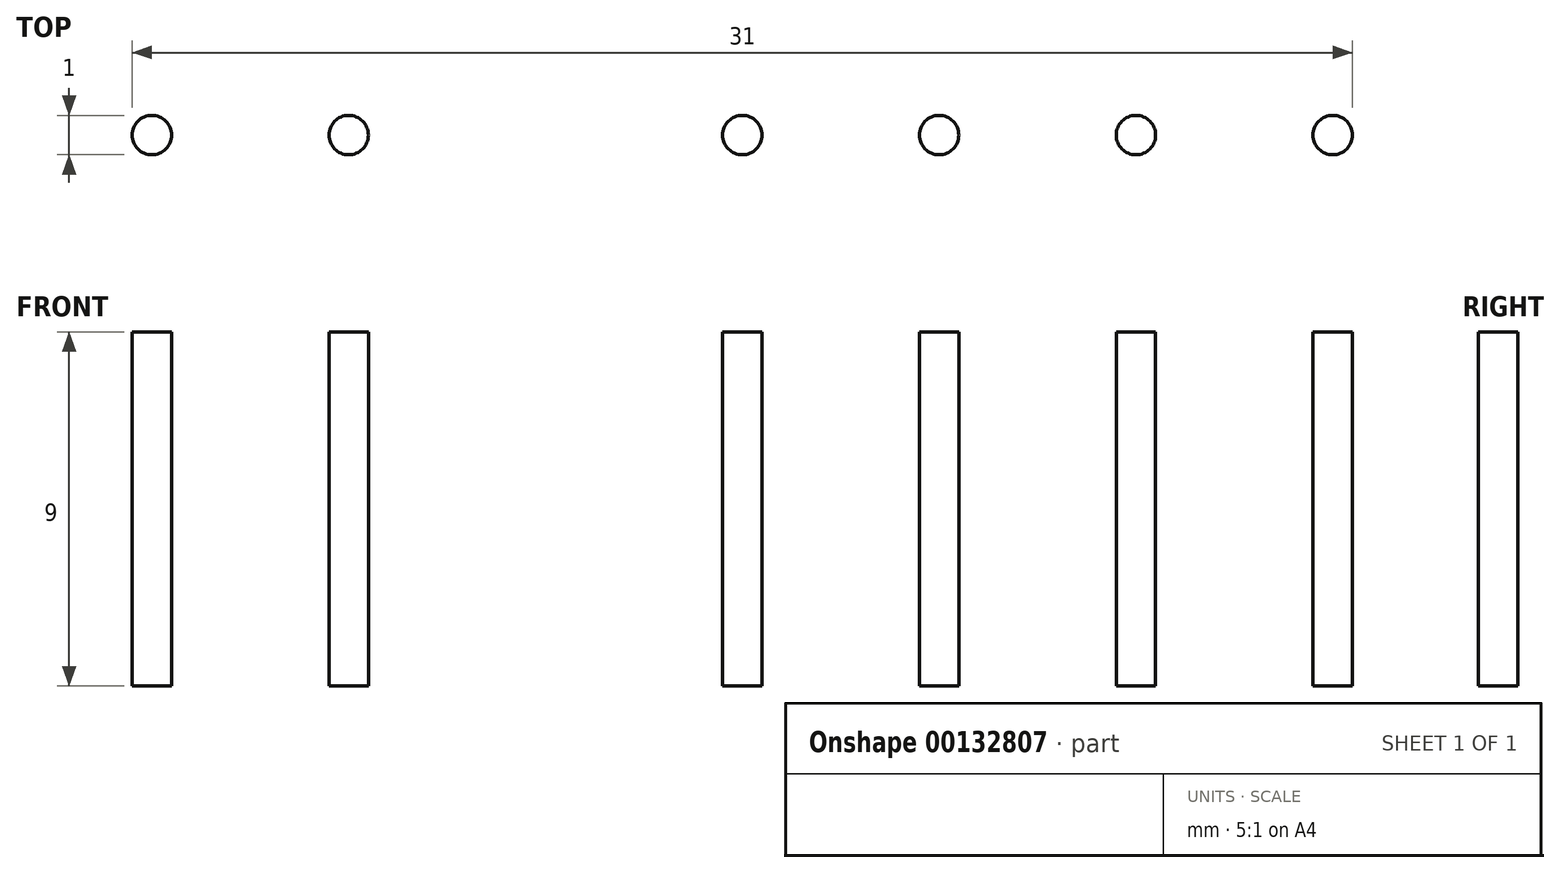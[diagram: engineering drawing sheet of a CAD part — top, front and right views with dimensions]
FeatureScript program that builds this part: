
annotation { "Feature Type Name" : "Feature", "Feature Type Description" : "" }
export const myFeature = defineFeature(function(context is Context, id is Id, definition is map)
    precondition{}
    {
        {
            var Q0;
            Q0=qCreatedBy(makeId("Top.planeOp"),FACE);
            var sketch = newSketch(context, id + "F0", { "sketchPlane" : qUnion([Q0])});
            skCircle(sketch, "E0", {"center": v(0, -20) * mm, "radius": 0.5 * mm});
            skCircle(sketch, "E1.1.0.0", {"center": v(5, -20) * mm, "radius": 0.5 * mm});
            skCircle(sketch, "E1.2.0.0", {"center": v(10, -20) * mm, "radius": 0.5 * mm});
            skCircle(sketch, "E1.3.0.0", {"center": v(15, -20) * mm, "radius": 0.5 * mm});
            skLineSegment(sketch, "E1.direction1", {"start": v(0, -20) * mm, "end": v(5, -20) * mm, "construction": true});
            skCircle(sketch, "E2.1.0.0", {"center": v(-5, -20) * mm, "radius": 0.5 * mm});
            skCircle(sketch, "E2.2.0.0", {"center": v(-10, -20) * mm, "radius": 0.5 * mm});
            skCircle(sketch, "E2.3.0.0", {"center": v(-15, -20) * mm, "radius": 0.5 * mm});
            skLineSegment(sketch, "E2.direction1", {"start": v(0, -20) * mm, "end": v(-5, -20) * mm, "construction": true});
            skCircle(sketch, "E3.MirrorC", {"center": v(0, 20) * mm, "radius": 0.5 * mm});
            skCircle(sketch, "E4.MirrorC", {"center": v(-5, 20) * mm, "radius": 0.5 * mm});
            skCircle(sketch, "E5.MirrorC", {"center": v(5, 20) * mm, "radius": 0.5 * mm});
            skCircle(sketch, "E6.MirrorC", {"center": v(10, 20) * mm, "radius": 0.5 * mm});
            skCircle(sketch, "E7.MirrorC", {"center": v(-15, 20) * mm, "radius": 0.5 * mm});
            skCircle(sketch, "E8.MirrorC", {"center": v(-10, 20) * mm, "radius": 0.5 * mm});
            skCircle(sketch, "E9.MirrorC", {"center": v(15, 20) * mm, "radius": 0.5 * mm});
            skLineSegment(sketch, "E10.MirrorCS", {"start": v(0, 20) * mm, "end": v(-5, 20) * mm, "construction": true});
            skLineSegment(sketch, "E11.MirrorCS", {"start": v(0, 20) * mm, "end": v(5, 20) * mm, "construction": true});
            skSolve(sketch);
        }
        {
            var Q0;
            Q0=makeQuery(id+"F0.imprint","IMPRINT",FACE,{"disambiguationData":[TD([[makeQuery(id+"F0.imprint","IMPRINT",EDGE,{"derivedFrom":sQuery(id+"F0.wireOp",EDGE,"E2.3.0.0")}),1.0]])]});
            var Q1;
            Q1=makeQuery(id+"F0.imprint","IMPRINT",FACE,{"disambiguationData":[TD([[makeQuery(id+"F0.imprint","IMPRINT",EDGE,{"derivedFrom":sQuery(id+"F0.wireOp",EDGE,"E2.2.0.0")}),1.0]])]});
            var Q2;
            Q2=makeQuery(id+"F0.imprint","IMPRINT",FACE,{"disambiguationData":[TD([[makeQuery(id+"F0.imprint","IMPRINT",EDGE,{"derivedFrom":sQuery(id+"F0.wireOp",EDGE,"E0")}),1.0]])]});
            var Q3;
            Q3=makeQuery(id+"F0.imprint","IMPRINT",FACE,{"disambiguationData":[TD([[makeQuery(id+"F0.imprint","IMPRINT",EDGE,{"derivedFrom":sQuery(id+"F0.wireOp",EDGE,"E1.1.0.0")}),1.0]])]});
            var Q4;
            Q4=makeQuery(id+"F0.imprint","IMPRINT",FACE,{"disambiguationData":[TD([[makeQuery(id+"F0.imprint","IMPRINT",EDGE,{"derivedFrom":sQuery(id+"F0.wireOp",EDGE,"E1.2.0.0")}),1.0]])]});
            var Q5;
            Q5=makeQuery(id+"F0.imprint","IMPRINT",FACE,{"disambiguationData":[TD([[makeQuery(id+"F0.imprint","IMPRINT",EDGE,{"derivedFrom":sQuery(id+"F0.wireOp",EDGE,"E1.3.0.0")}),1.0]])]});
            var Q6;
            Q6=makeQuery(id+"F0.imprint","IMPRINT",FACE,{"disambiguationData":[TD([[makeQuery(id+"F0.imprint","IMPRINT",EDGE,{"derivedFrom":sQuery(id+"F0.wireOp",EDGE,"E9.MirrorC")}),-1.0]])]});
            var Q7;
            Q7=makeQuery(id+"F0.imprint","IMPRINT",FACE,{"disambiguationData":[TD([[makeQuery(id+"F0.imprint","IMPRINT",EDGE,{"derivedFrom":sQuery(id+"F0.wireOp",EDGE,"E5.MirrorC")}),-1.0]])]});
            var Q8;
            Q8=makeQuery(id+"F0.imprint","IMPRINT",FACE,{"disambiguationData":[TD([[makeQuery(id+"F0.imprint","IMPRINT",EDGE,{"derivedFrom":sQuery(id+"F0.wireOp",EDGE,"E6.MirrorC")}),-1.0]])]});
            var Q9;
            Q9=makeQuery(id+"F0.imprint","IMPRINT",FACE,{"disambiguationData":[TD([[makeQuery(id+"F0.imprint","IMPRINT",EDGE,{"derivedFrom":sQuery(id+"F0.wireOp",EDGE,"E4.MirrorC")}),-1.0]])]});
            var Q10;
            Q10=makeQuery(id+"F0.imprint","IMPRINT",FACE,{"disambiguationData":[TD([[makeQuery(id+"F0.imprint","IMPRINT",EDGE,{"derivedFrom":sQuery(id+"F0.wireOp",EDGE,"E7.MirrorC")}),-1.0]])]});
            var Q11;
            Q11=makeQuery(id+"F0.imprint","IMPRINT",FACE,{"disambiguationData":[TD([[makeQuery(id+"F0.imprint","IMPRINT",EDGE,{"derivedFrom":sQuery(id+"F0.wireOp",EDGE,"E8.MirrorC")}),-1.0]])]});
            extrude(context, id + "F1", {"entities" : qUnion([Q0, Q1, Q2, Q3, Q4, Q5, Q6, Q7, Q8, Q9, Q10, Q11]), "depth" : 5 * mm, "hasSecondDirection" : true, "secondDirectionOppositeDirection" : true, "secondDirectionDepth" : 4 * mm});
        }
    });
